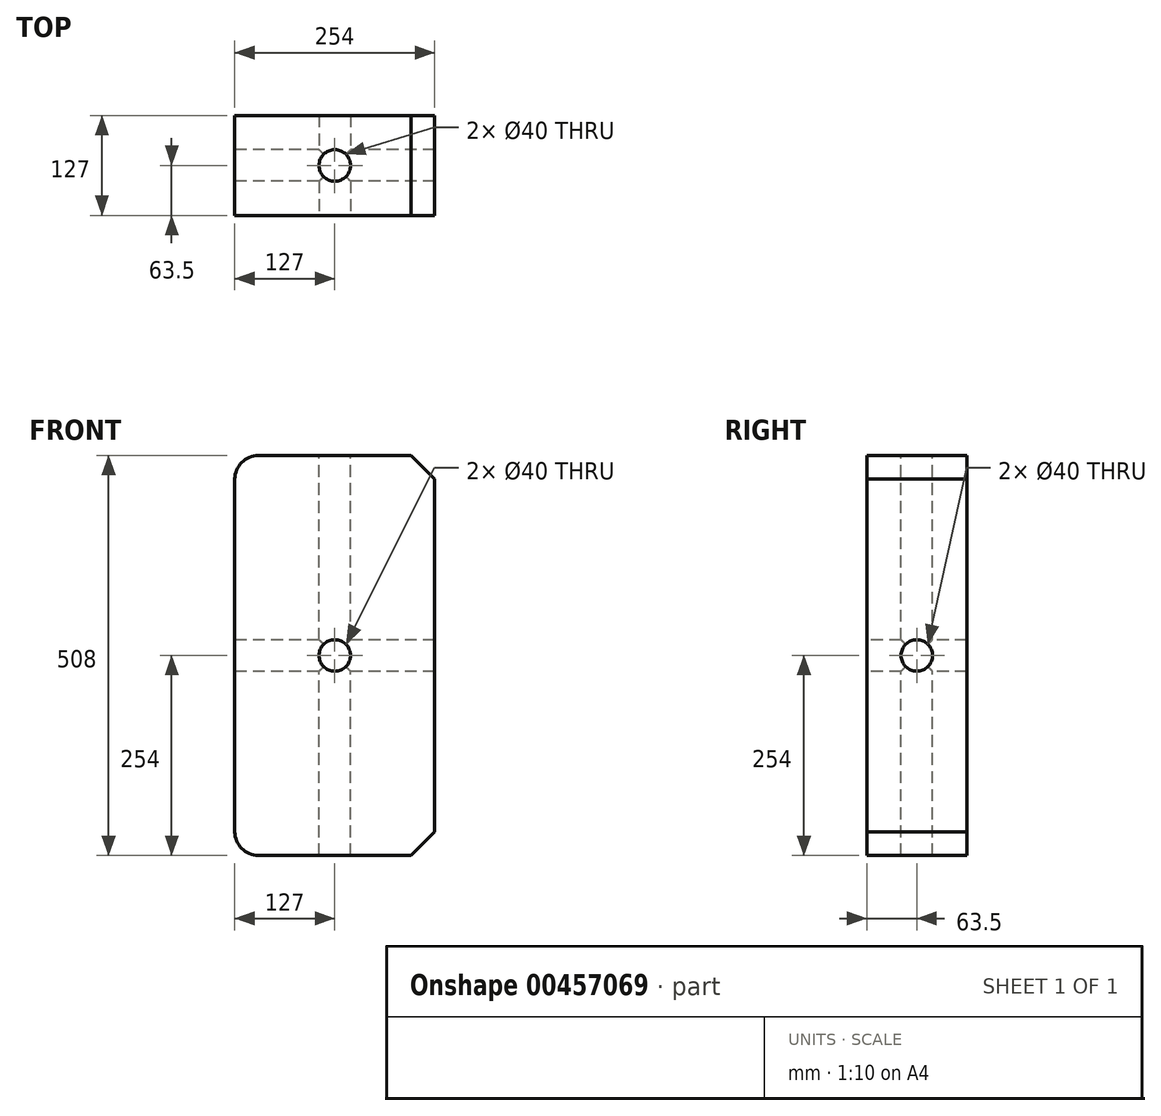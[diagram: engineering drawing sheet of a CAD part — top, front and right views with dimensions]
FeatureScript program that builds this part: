
annotation { "Feature Type Name" : "Feature", "Feature Type Description" : "" }
export const myFeature = defineFeature(function(context is Context, id is Id, definition is map)
    precondition{}
    {
        {
            var Q0;
            Q0=qCreatedBy(makeId("Front.planeOp"),FACE);
            var sketch = newSketch(context, id + "F0", { "sketchPlane" : qUnion([Q0])});
            skLineSegment(sketch, "E0.bottom", {"start": v(-127, -254) * mm, "end": v(127, -254) * mm});
            skLineSegment(sketch, "E0.top", {"start": v(-127, 254) * mm, "end": v(127, 254) * mm});
            skLineSegment(sketch, "E0.left", {"start": v(-127, -254) * mm, "end": v(-127, 254) * mm});
            skLineSegment(sketch, "E0.right", {"start": v(127, -254) * mm, "end": v(127, 254) * mm});
            skPoint(sketch, "E0.middle", {"position": v(0, 0) * mm});
            skSolve(sketch);
        }
        {
            var Q0;
            Q0=makeQuery(id+"F0.imprint","IMPRINT",FACE,{"disambiguationData":[TD([[makeQuery(id+"F0.imprint","IMPRINT",EDGE,{"derivedFrom":sQuery(id+"F0.wireOp",EDGE,"E0.bottom")}),1.0]])]});
            extrude(context, id + "F1", {"entities" : qUnion([Q0]), "depth" : 127 * mm});
        }
        {
            var Q0;
            Q0=makeQuery(id+"F1.opExtrude","CAP_FACE",FACE,{"disambiguationData":[OSD([sQuery(id+"F0.wireOp",EDGE,"E0.bottom"),sQuery(id+"F0.wireOp",EDGE,"E0.top"),sQuery(id+"F0.wireOp",EDGE,"E0.left"),sQuery(id+"F0.wireOp",EDGE,"E0.right")])],"isStart":false});
            var sketch = newSketch(context, id + "F2", { "sketchPlane" : qUnion([Q0])});
            skCircle(sketch, "E1", {"center": v(0, 0) * mm, "radius": 20 * mm});
            skSolve(sketch);
        }
        {
            var Q0;
            Q0=makeQuery(id+"F1.opExtrude","SWEPT_EDGE",EDGE,{"disambiguationData":[OSD([sQuery(id+"F0.wireOp",EDGE,"E0.top"),sQuery(id+"F0.wireOp",EDGE,"E0.right")])]});
            var Q1;
            Q1=makeQuery(id+"F1.opExtrude","SWEPT_EDGE",EDGE,{"disambiguationData":[OSD([sQuery(id+"F0.wireOp",EDGE,"E0.bottom"),sQuery(id+"F0.wireOp",EDGE,"E0.right")])]});
            chamfer(context, id + "F3", {"entities" : qUnion([Q0, Q1]), "width" : 30 * mm, "tangentPropagation" : true});
        }
        {
            var Q0;
            Q0=makeQuery(id+"F1.opExtrude","SWEPT_EDGE",EDGE,{"disambiguationData":[OSD([sQuery(id+"F0.wireOp",EDGE,"E0.top"),sQuery(id+"F0.wireOp",EDGE,"E0.left")])]});
            var Q1;
            Q1=makeQuery(id+"F1.opExtrude","SWEPT_EDGE",EDGE,{"disambiguationData":[OSD([sQuery(id+"F0.wireOp",EDGE,"E0.bottom"),sQuery(id+"F0.wireOp",EDGE,"E0.left")])]});
            fillet(context, id + "F4", {"entities" : qUnion([Q0, Q1]), "radius" : 30 * mm, "tangentPropagation" : true, "allowEdgeOverflow" : false});
        }
        {
            var Q0;
            Q0 = qSketchRegion(id + "F2", true);
            extrude(context, id + "F5", {"entities" : qUnion([Q0]), "operationType" : NewBodyOperationType.REMOVE, "endBound" : BoundingType.THROUGH_ALL, "oppositeDirection" : true, "depth" : 25 * mm});
        }
        {
            var Q0;
            Q0=makeQuery(id+"F1.opExtrude","SWEPT_FACE",FACE,{"disambiguationData":[OSD([sQuery(id+"F0.wireOp",EDGE,"E0.left")])]});
            var sketch = newSketch(context, id + "F6", { "sketchPlane" : qUnion([Q0])});
            skCircle(sketch, "E2", {"center": v(63.5, 0) * mm, "radius": 20 * mm});
            skPoint(sketch, "E2.centerSnap0", {"position": v(63.5, -224) * mm});
            skSolve(sketch);
        }
        {
            var Q0;
            Q0=makeQuery(id+"F6.imprint","IMPRINT",FACE,{"disambiguationData":[TD([[makeQuery(id+"F6.imprint","IMPRINT",EDGE,{"derivedFrom":sQuery(id+"F6.wireOp",EDGE,"E2")}),1.0]])]});
            extrude(context, id + "F7", {"entities" : qUnion([Q0]), "operationType" : NewBodyOperationType.REMOVE, "endBound" : BoundingType.THROUGH_ALL, "oppositeDirection" : true, "depth" : 25 * mm});
        }
        {
            var Q0;
            Q0=makeQuery(id+"F1.opExtrude","SWEPT_FACE",FACE,{"disambiguationData":[OSD([sQuery(id+"F0.wireOp",EDGE,"E0.top")])]});
            var sketch = newSketch(context, id + "F8", { "sketchPlane" : qUnion([Q0])});
            skCircle(sketch, "E3", {"center": v(0, -63.5) * mm, "radius": 20 * mm});
            skPoint(sketch, "E3.centerSnap0", {"position": v(-97, -63.5) * mm});
            skSolve(sketch);
        }
        {
            var Q0;
            Q0=makeQuery(id+"F8.imprint","IMPRINT",FACE,{"disambiguationData":[TD([[makeQuery(id+"F8.imprint","IMPRINT",EDGE,{"derivedFrom":sQuery(id+"F8.wireOp",EDGE,"E3")}),1.0]])]});
            extrude(context, id + "F9", {"entities" : qUnion([Q0]), "operationType" : NewBodyOperationType.REMOVE, "endBound" : BoundingType.THROUGH_ALL, "oppositeDirection" : true, "depth" : 25 * mm});
        }
    });
